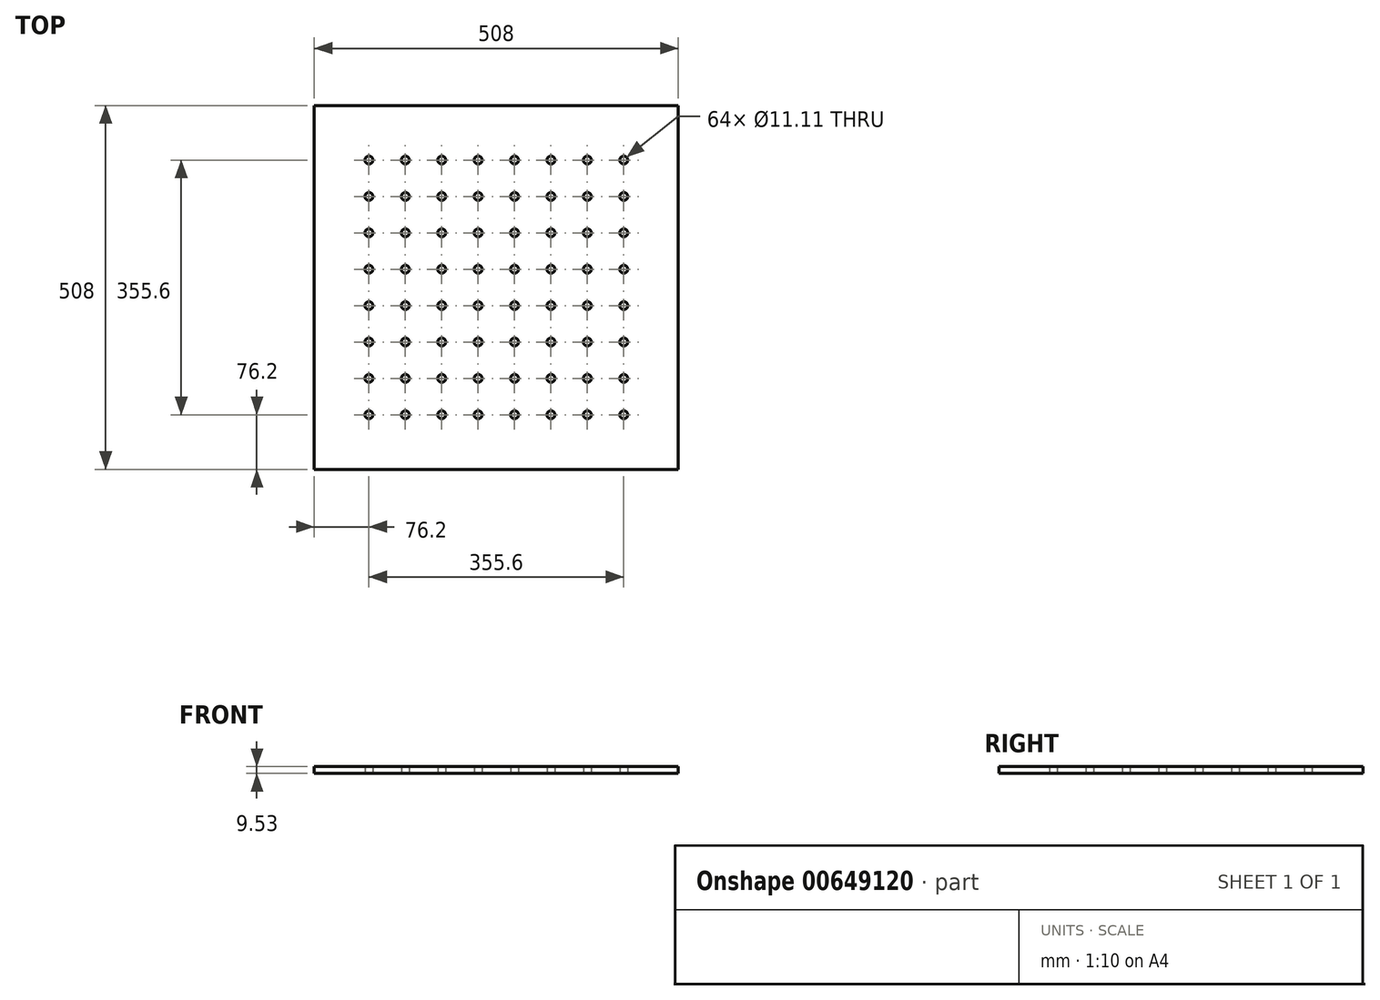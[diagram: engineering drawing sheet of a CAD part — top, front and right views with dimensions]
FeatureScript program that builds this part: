
annotation { "Feature Type Name" : "Feature", "Feature Type Description" : "" }
export const myFeature = defineFeature(function(context is Context, id is Id, definition is map)
    precondition{}
    {
        {
            var Q0;
            Q0=qCreatedBy(makeId("Top.planeOp"),FACE);
            var sketch = newSketch(context, id + "F0", { "sketchPlane" : qUnion([Q0])});
            skLineSegment(sketch, "E0.bottom", {"start": v(0, 0) * mm, "end": v(508, 0) * mm});
            skLineSegment(sketch, "E0.top", {"start": v(0, 508) * mm, "end": v(508, 508) * mm});
            skLineSegment(sketch, "E0.left", {"start": v(0, 0) * mm, "end": v(0, 508) * mm});
            skLineSegment(sketch, "E0.right", {"start": v(508, 0) * mm, "end": v(508, 508) * mm});
            skCircle(sketch, "E1", {"center": v(76.2, 76.2) * mm, "radius": 5.56 * mm});
            skCircle(sketch, "E2.0.1.0", {"center": v(76.2, 127) * mm, "radius": 5.56 * mm});
            skCircle(sketch, "E2.0.2.0", {"center": v(76.2, 177.8) * mm, "radius": 5.56 * mm});
            skCircle(sketch, "E2.0.3.0", {"center": v(76.2, 228.6) * mm, "radius": 5.56 * mm});
            skCircle(sketch, "E2.0.4.0", {"center": v(76.2, 279.4) * mm, "radius": 5.56 * mm});
            skCircle(sketch, "E2.0.5.0", {"center": v(76.2, 330.2) * mm, "radius": 5.56 * mm});
            skCircle(sketch, "E2.0.6.0", {"center": v(76.2, 381) * mm, "radius": 5.56 * mm});
            skCircle(sketch, "E2.0.7.0", {"center": v(76.2, 431.8) * mm, "radius": 5.56 * mm});
            skCircle(sketch, "E2.1.0.0", {"center": v(127, 76.2) * mm, "radius": 5.56 * mm});
            skCircle(sketch, "E2.1.1.0", {"center": v(127, 127) * mm, "radius": 5.56 * mm});
            skCircle(sketch, "E2.1.2.0", {"center": v(127, 177.8) * mm, "radius": 5.56 * mm});
            skCircle(sketch, "E2.1.3.0", {"center": v(127, 228.6) * mm, "radius": 5.56 * mm});
            skCircle(sketch, "E2.1.4.0", {"center": v(127, 279.4) * mm, "radius": 5.56 * mm});
            skCircle(sketch, "E2.1.5.0", {"center": v(127, 330.2) * mm, "radius": 5.56 * mm});
            skCircle(sketch, "E2.1.6.0", {"center": v(127, 381) * mm, "radius": 5.56 * mm});
            skCircle(sketch, "E2.1.7.0", {"center": v(127, 431.8) * mm, "radius": 5.56 * mm});
            skCircle(sketch, "E2.2.0.0", {"center": v(177.8, 76.2) * mm, "radius": 5.56 * mm});
            skCircle(sketch, "E2.2.1.0", {"center": v(177.8, 127) * mm, "radius": 5.56 * mm});
            skCircle(sketch, "E2.2.2.0", {"center": v(177.8, 177.8) * mm, "radius": 5.56 * mm});
            skCircle(sketch, "E2.2.3.0", {"center": v(177.8, 228.6) * mm, "radius": 5.56 * mm});
            skCircle(sketch, "E2.2.4.0", {"center": v(177.8, 279.4) * mm, "radius": 5.56 * mm});
            skCircle(sketch, "E2.2.5.0", {"center": v(177.8, 330.2) * mm, "radius": 5.56 * mm});
            skCircle(sketch, "E2.2.6.0", {"center": v(177.8, 381) * mm, "radius": 5.56 * mm});
            skCircle(sketch, "E2.2.7.0", {"center": v(177.8, 431.8) * mm, "radius": 5.56 * mm});
            skCircle(sketch, "E2.3.0.0", {"center": v(228.6, 76.2) * mm, "radius": 5.56 * mm});
            skCircle(sketch, "E2.3.1.0", {"center": v(228.6, 127) * mm, "radius": 5.56 * mm});
            skCircle(sketch, "E2.3.2.0", {"center": v(228.6, 177.8) * mm, "radius": 5.56 * mm});
            skCircle(sketch, "E2.3.3.0", {"center": v(228.6, 228.6) * mm, "radius": 5.56 * mm});
            skCircle(sketch, "E2.3.4.0", {"center": v(228.6, 279.4) * mm, "radius": 5.56 * mm});
            skCircle(sketch, "E2.3.5.0", {"center": v(228.6, 330.2) * mm, "radius": 5.56 * mm});
            skCircle(sketch, "E2.3.6.0", {"center": v(228.6, 381) * mm, "radius": 5.56 * mm});
            skCircle(sketch, "E2.3.7.0", {"center": v(228.6, 431.8) * mm, "radius": 5.56 * mm});
            skCircle(sketch, "E2.4.0.0", {"center": v(279.4, 76.2) * mm, "radius": 5.56 * mm});
            skCircle(sketch, "E2.4.1.0", {"center": v(279.4, 127) * mm, "radius": 5.56 * mm});
            skCircle(sketch, "E2.4.2.0", {"center": v(279.4, 177.8) * mm, "radius": 5.56 * mm});
            skCircle(sketch, "E2.4.3.0", {"center": v(279.4, 228.6) * mm, "radius": 5.56 * mm});
            skCircle(sketch, "E2.4.4.0", {"center": v(279.4, 279.4) * mm, "radius": 5.56 * mm});
            skCircle(sketch, "E2.4.5.0", {"center": v(279.4, 330.2) * mm, "radius": 5.56 * mm});
            skCircle(sketch, "E2.4.6.0", {"center": v(279.4, 381) * mm, "radius": 5.56 * mm});
            skCircle(sketch, "E2.4.7.0", {"center": v(279.4, 431.8) * mm, "radius": 5.56 * mm});
            skCircle(sketch, "E2.5.0.0", {"center": v(330.2, 76.2) * mm, "radius": 5.56 * mm});
            skCircle(sketch, "E2.5.1.0", {"center": v(330.2, 127) * mm, "radius": 5.56 * mm});
            skCircle(sketch, "E2.5.2.0", {"center": v(330.2, 177.8) * mm, "radius": 5.56 * mm});
            skCircle(sketch, "E2.5.3.0", {"center": v(330.2, 228.6) * mm, "radius": 5.56 * mm});
            skCircle(sketch, "E2.5.4.0", {"center": v(330.2, 279.4) * mm, "radius": 5.56 * mm});
            skCircle(sketch, "E2.5.5.0", {"center": v(330.2, 330.2) * mm, "radius": 5.56 * mm});
            skCircle(sketch, "E2.5.6.0", {"center": v(330.2, 381) * mm, "radius": 5.56 * mm});
            skCircle(sketch, "E2.5.7.0", {"center": v(330.2, 431.8) * mm, "radius": 5.56 * mm});
            skCircle(sketch, "E2.6.0.0", {"center": v(381, 76.2) * mm, "radius": 5.56 * mm});
            skCircle(sketch, "E2.6.1.0", {"center": v(381, 127) * mm, "radius": 5.56 * mm});
            skCircle(sketch, "E2.6.2.0", {"center": v(381, 177.8) * mm, "radius": 5.56 * mm});
            skCircle(sketch, "E2.6.3.0", {"center": v(381, 228.6) * mm, "radius": 5.56 * mm});
            skCircle(sketch, "E2.6.4.0", {"center": v(381, 279.4) * mm, "radius": 5.56 * mm});
            skCircle(sketch, "E2.6.5.0", {"center": v(381, 330.2) * mm, "radius": 5.56 * mm});
            skCircle(sketch, "E2.6.6.0", {"center": v(381, 381) * mm, "radius": 5.56 * mm});
            skCircle(sketch, "E2.6.7.0", {"center": v(381, 431.8) * mm, "radius": 5.56 * mm});
            skCircle(sketch, "E2.7.0.0", {"center": v(431.8, 76.2) * mm, "radius": 5.56 * mm});
            skCircle(sketch, "E2.7.1.0", {"center": v(431.8, 127) * mm, "radius": 5.56 * mm});
            skCircle(sketch, "E2.7.2.0", {"center": v(431.8, 177.8) * mm, "radius": 5.56 * mm});
            skCircle(sketch, "E2.7.3.0", {"center": v(431.8, 228.6) * mm, "radius": 5.56 * mm});
            skCircle(sketch, "E2.7.4.0", {"center": v(431.8, 279.4) * mm, "radius": 5.56 * mm});
            skCircle(sketch, "E2.7.5.0", {"center": v(431.8, 330.2) * mm, "radius": 5.56 * mm});
            skCircle(sketch, "E2.7.6.0", {"center": v(431.8, 381) * mm, "radius": 5.56 * mm});
            skCircle(sketch, "E2.7.7.0", {"center": v(431.8, 431.8) * mm, "radius": 5.56 * mm});
            skLineSegment(sketch, "E2.direction1", {"start": v(76.2, 76.2) * mm, "end": v(127, 76.2) * mm, "construction": true});
            skLineSegment(sketch, "E2.direction2", {"start": v(76.2, 76.2) * mm, "end": v(76.2, 127) * mm, "construction": true});
            skSolve(sketch);
        }
        {
            var Q0;
            Q0 = qSketchRegion(id + "F0", true);
            extrude(context, id + "F1", {"entities" : qUnion([Q0]), "flatOperationType" : FlatOperationType.REMOVE, "depth" : 9.52 * mm, "offsetDistance" : 25.4 * mm, "domain" : OperationDomain.MODEL});
        }
    });
